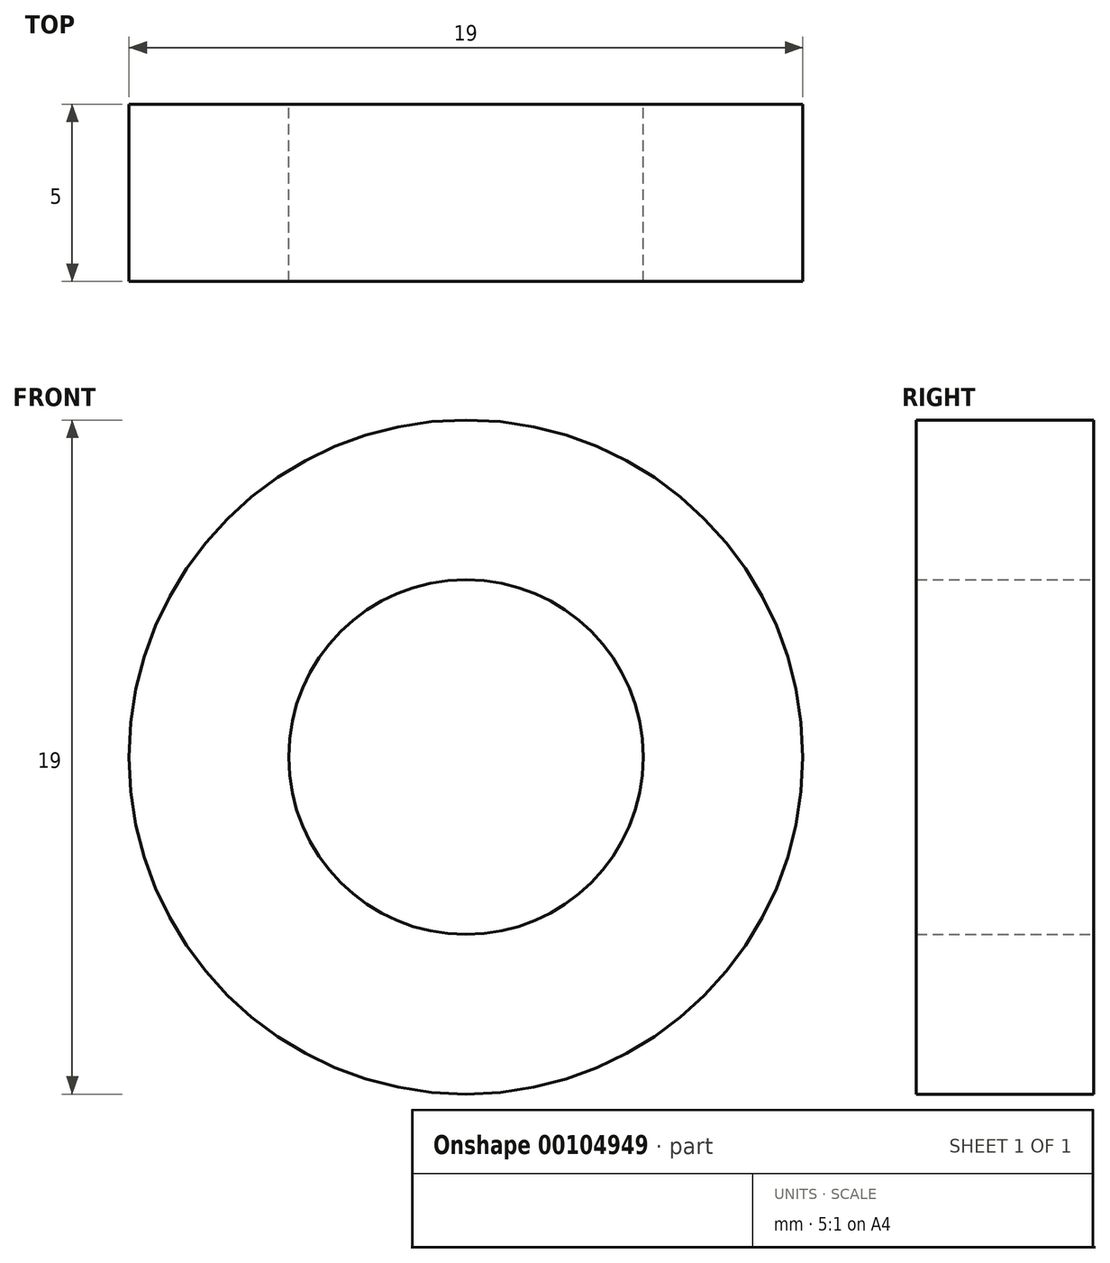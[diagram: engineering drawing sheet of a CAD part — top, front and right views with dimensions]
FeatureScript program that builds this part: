
annotation { "Feature Type Name" : "Feature", "Feature Type Description" : "" }
export const myFeature = defineFeature(function(context is Context, id is Id, definition is map)
    precondition{}
    {
        {
            var Q0;
            Q0=qCreatedBy(makeId("Front.planeOp"),FACE);
            var sketch = newSketch(context, id + "F0", { "sketchPlane" : qUnion([Q0])});
            skCircle(sketch, "E0", {"center": v(0, 0) * mm, "radius": 9.5 * mm});
            skCircle(sketch, "E1", {"center": v(0, 0) * mm, "radius": 5 * mm});
            skSolve(sketch);
        }
        {
            var Q0;
            Q0 = qSketchRegion(id + "F0", true);
            extrude(context, id + "F1", {"entities" : qUnion([Q0]), "depth" : 5 * mm});
        }
    });
